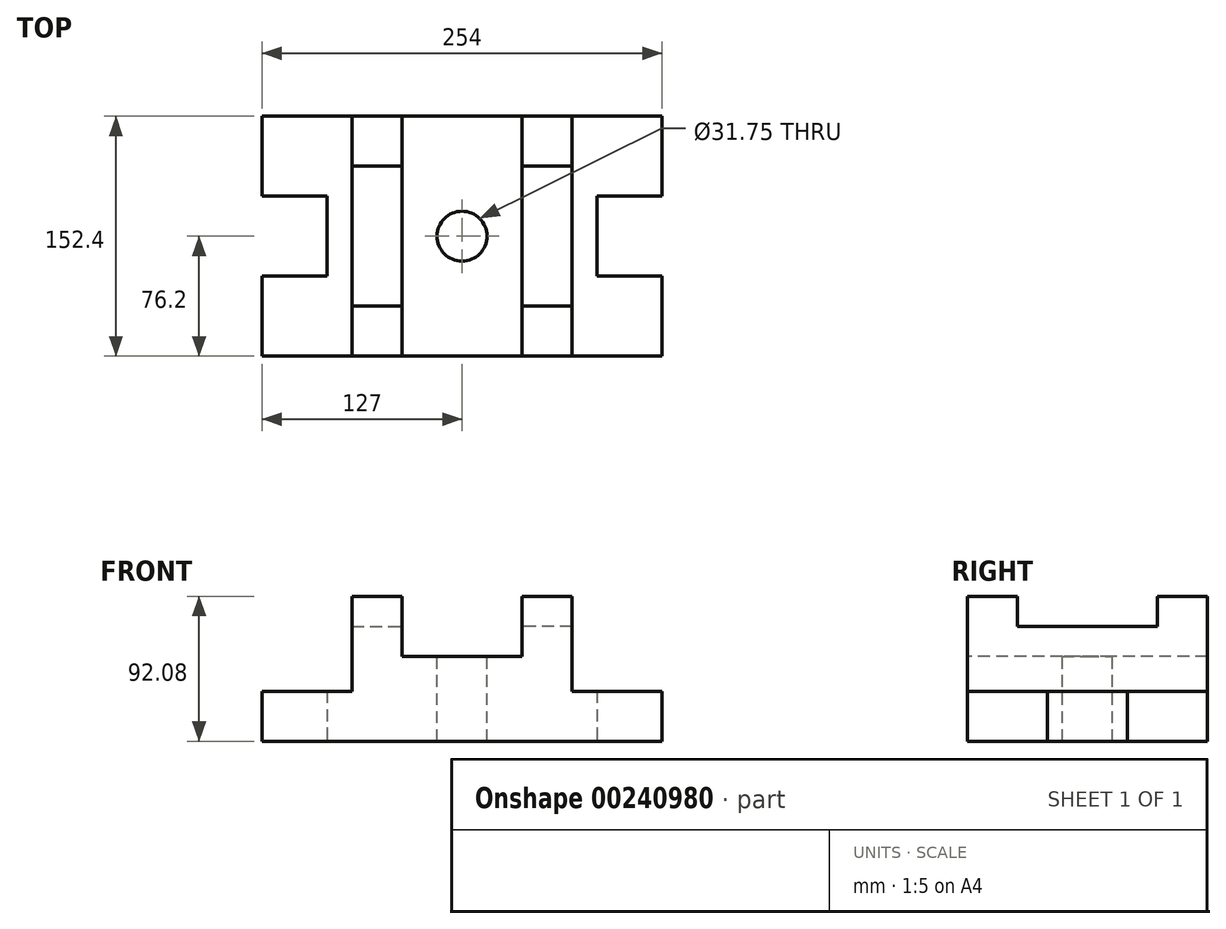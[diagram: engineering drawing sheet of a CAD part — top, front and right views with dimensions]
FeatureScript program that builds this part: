
annotation { "Feature Type Name" : "Feature", "Feature Type Description" : "" }
export const myFeature = defineFeature(function(context is Context, id is Id, definition is map)
    precondition{}
    {
        {
            var Q0;
            Q0=qCreatedBy(makeId("Top.planeOp"),FACE);
            var sketch = newSketch(context, id + "F0", { "sketchPlane" : qUnion([Q0])});
            skLineSegment(sketch, "E0.top", {"start": v(0, -76.2) * mm, "end": v(127, -76.2) * mm});
            skLineSegment(sketch, "E0.right", {"start": v(127, -25.4) * mm, "end": v(127, -76.2) * mm});
            skLineSegment(sketch, "E1.MirrorCS", {"start": v(0, 76.2) * mm, "end": v(127, 76.2) * mm});
            skLineSegment(sketch, "E2.MirrorCS", {"start": v(127, 25.4) * mm, "end": v(127, 76.2) * mm});
            skPoint(sketch, "E3", {"position": v(85.73, 0) * mm});
            skLineSegment(sketch, "E4.bottom", {"start": v(127, 25.4) * mm, "end": v(85.72, 25.4) * mm});
            skLineSegment(sketch, "E4.top", {"start": v(127, -25.4) * mm, "end": v(85.73, -25.4) * mm});
            skLineSegment(sketch, "E4.right", {"start": v(85.72, 25.4) * mm, "end": v(85.73, -25.4) * mm});
            skLineSegment(sketch, "E5.MirrorCS", {"start": v(0, 76.2) * mm, "end": v(-127, 76.2) * mm});
            skLineSegment(sketch, "E6.MirrorCS", {"start": v(0, -76.2) * mm, "end": v(-127, -76.2) * mm});
            skLineSegment(sketch, "E7.MirrorCS", {"start": v(-127, 25.4) * mm, "end": v(-127, 76.2) * mm});
            skLineSegment(sketch, "E8.MirrorCS", {"start": v(-85.72, 25.4) * mm, "end": v(-85.73, -25.4) * mm});
            skLineSegment(sketch, "E9.MirrorCS", {"start": v(-127, 25.4) * mm, "end": v(-85.72, 25.4) * mm});
            skLineSegment(sketch, "E10.MirrorCS", {"start": v(-127, -25.4) * mm, "end": v(-85.73, -25.4) * mm});
            skLineSegment(sketch, "E11.MirrorCS", {"start": v(-127, -25.4) * mm, "end": v(-127, -76.2) * mm});
            skLineSegment(sketch, "E12.bottom", {"start": v(69.85, -76.2) * mm, "end": v(-69.85, -76.2) * mm});
            skPoint(sketch, "E12.middle", {"position": v(0, 0) * mm});
            skSolve(sketch);
        }
        {
            var Q0;
            Q0 = qSketchRegion(id + "F0", true);
            extrude(context, id + "F1", {"entities" : qUnion([Q0]), "depth" : 31.75 * mm});
        }
        {
            var Q0;
            Q0=makeQuery(id+"F1.opExtrude","CAP_FACE",FACE,{"disambiguationData":[OSD([sQuery(id+"F0.wireOp",EDGE,"pTGMPnu9-1J7j-vLpY-UZ5C-XiEDzq8Ojeuh"),sQuery(id+"F0.wireOp",EDGE,"E0.top"),sQuery(id+"F0.wireOp",EDGE,"E0.right"),sQuery(id+"F0.wireOp",EDGE,"E1.MirrorCS"),sQuery(id+"F0.wireOp",EDGE,"E2.MirrorCS"),sQuery(id+"F0.wireOp",EDGE,"E4.bottom"),sQuery(id+"F0.wireOp",EDGE,"E4.top"),sQuery(id+"F0.wireOp",EDGE,"E4.right"),sQuery(id+"F0.wireOp",EDGE,"E5.MirrorCS"),sQuery(id+"F0.wireOp",EDGE,"E6.MirrorCS"),sQuery(id+"F0.wireOp",EDGE,"E7.MirrorCS"),sQuery(id+"F0.wireOp",EDGE,"E8.MirrorCS"),sQuery(id+"F0.wireOp",EDGE,"E9.MirrorCS"),sQuery(id+"F0.wireOp",EDGE,"E10.MirrorCS"),sQuery(id+"F0.wireOp",EDGE,"E11.MirrorCS"),sQuery(id+"F0.wireOp",EDGE,"E12.bottom")])],"isStart":false});
            var sketch = newSketch(context, id + "F2", { "sketchPlane" : qUnion([Q0])});
            skLineSegment(sketch, "E13.bottom", {"start": v(69.85, -76.2) * mm, "end": v(-69.85, -76.2) * mm});
            skLineSegment(sketch, "E13.top", {"start": v(69.85, 76.2) * mm, "end": v(-69.85, 76.2) * mm});
            skLineSegment(sketch, "E13.left", {"start": v(69.85, -76.2) * mm, "end": v(69.85, 76.2) * mm});
            skLineSegment(sketch, "E13.right", {"start": v(-69.85, -76.2) * mm, "end": v(-69.85, 76.2) * mm});
            skPoint(sketch, "E13.middle", {"position": v(0, 0) * mm});
            skSolve(sketch);
        }
        {
            var Q0;
            Q0 = qSketchRegion(id + "F2", true);
            var Q1;
            Q1=sQuery(id+"F2.wireOp",EDGE,"E13.right");
            var Q2;
            Q2=sQuery(id+"F2.wireOp",EDGE,"E13.top");
            var Q3;
            Q3=sQuery(id+"F2.wireOp",EDGE,"E13.left");
            var Q4;
            Q4=sQuery(id+"F2.wireOp",EDGE,"E13.bottom");
            extrude(context, id + "F3", {"entities" : qUnion([Q0]), "operationType" : NewBodyOperationType.ADD, "surfaceEntities" : qUnion([Q1, Q2, Q3, Q4]), "depth" : 22.22 * mm});
        }
        {
            var Q0;
            Q0=makeQuery(id+"F3.opExtrude","CAP_FACE",FACE,{"disambiguationData":[OSD([sQuery(id+"F2.wireOp",EDGE,"E13.bottom"),sQuery(id+"F2.wireOp",EDGE,"E13.top"),sQuery(id+"F2.wireOp",EDGE,"E13.left"),sQuery(id+"F2.wireOp",EDGE,"E13.right")])],"isStart":false});
            var sketch = newSketch(context, id + "F4", { "sketchPlane" : qUnion([Q0])});
            skLineSegment(sketch, "E14.bottom", {"start": v(69.85, 76.2) * mm, "end": v(38.1, 76.2) * mm});
            skLineSegment(sketch, "E14.top", {"start": v(69.85, -76.2) * mm, "end": v(38.1, -76.2) * mm});
            skLineSegment(sketch, "E14.left", {"start": v(69.85, 76.2) * mm, "end": v(69.85, -76.2) * mm});
            skLineSegment(sketch, "E14.right", {"start": v(38.1, 76.2) * mm, "end": v(38.1, -76.2) * mm});
            skLineSegment(sketch, "E15.MirrorCS", {"start": v(-38.1, 76.2) * mm, "end": v(-38.1, -76.2) * mm});
            skLineSegment(sketch, "E16.MirrorCS", {"start": v(-69.85, 76.2) * mm, "end": v(-38.1, 76.2) * mm});
            skLineSegment(sketch, "E17.MirrorCS", {"start": v(-69.85, 76.2) * mm, "end": v(-69.85, -76.2) * mm});
            skLineSegment(sketch, "E18.MirrorCS", {"start": v(-69.85, -76.2) * mm, "end": v(-38.1, -76.2) * mm});
            skSolve(sketch);
        }
        {
            var Q0;
            Q0 = qSketchRegion(id + "F4", true);
            extrude(context, id + "F5", {"entities" : qUnion([Q0]), "operationType" : NewBodyOperationType.ADD, "depth" : 19.05 * mm});
        }
        {
            var Q0;
            Q0=makeQuery(id+"F5.opExtrude","CAP_FACE",FACE,{"disambiguationData":[OSD([sQuery(id+"F4.wireOp",EDGE,"E14.bottom"),sQuery(id+"F4.wireOp",EDGE,"E14.top"),sQuery(id+"F4.wireOp",EDGE,"E14.left"),sQuery(id+"F4.wireOp",EDGE,"E14.right")])],"isStart":false});
            var sketch = newSketch(context, id + "F6", { "sketchPlane" : qUnion([Q0])});
            skLineSegment(sketch, "E19", {"start": v(38.1, -76.2) * mm, "end": v(69.85, -76.2) * mm});
            skLineSegment(sketch, "E20", {"start": v(69.85, -76.2) * mm, "end": v(69.85, -44.45) * mm});
            skLineSegment(sketch, "E21", {"start": v(69.85, -44.45) * mm, "end": v(38.1, -44.45) * mm});
            skLineSegment(sketch, "E22", {"start": v(38.1, -44.45) * mm, "end": v(38.1, -76.2) * mm});
            skLineSegment(sketch, "E23.MirrorCS", {"start": v(-69.85, -44.45) * mm, "end": v(-38.1, -44.45) * mm});
            skLineSegment(sketch, "E24.MirrorCS", {"start": v(-38.1, -44.45) * mm, "end": v(-38.1, -76.2) * mm});
            skLineSegment(sketch, "E25.MirrorCS", {"start": v(-69.85, -76.2) * mm, "end": v(-69.85, -44.45) * mm});
            skLineSegment(sketch, "E26.MirrorCS", {"start": v(-38.1, -76.2) * mm, "end": v(-69.85, -76.2) * mm});
            skLineSegment(sketch, "E27.MirrorCS", {"start": v(69.85, 44.45) * mm, "end": v(38.1, 44.45) * mm});
            skLineSegment(sketch, "E28.MirrorCS", {"start": v(69.85, 76.2) * mm, "end": v(69.85, 44.45) * mm});
            skLineSegment(sketch, "E29.MirrorCS", {"start": v(38.1, 76.2) * mm, "end": v(69.85, 76.2) * mm});
            skLineSegment(sketch, "E30.MirrorCS", {"start": v(38.1, 44.45) * mm, "end": v(38.1, 76.2) * mm});
            skLineSegment(sketch, "E31.MirrorCS", {"start": v(-69.85, 44.45) * mm, "end": v(-38.1, 44.45) * mm});
            skLineSegment(sketch, "E32.MirrorCS", {"start": v(-38.1, 44.45) * mm, "end": v(-38.1, 76.2) * mm});
            skLineSegment(sketch, "E33.MirrorCS", {"start": v(-69.85, 76.2) * mm, "end": v(-69.85, 44.45) * mm});
            skLineSegment(sketch, "E34", {"start": v(-69.85, 76.2) * mm, "end": v(-38.1, 76.2) * mm});
            skLineSegment(sketch, "E35", {"start": v(-69.85, -76.2) * mm, "end": v(-38.1, -76.2) * mm});
            skSolve(sketch);
        }
        {
            var Q0;
            Q0 = qSketchRegion(id + "F6", true);
            extrude(context, id + "F7", {"entities" : qUnion([Q0]), "operationType" : NewBodyOperationType.ADD, "depth" : 19.05 * mm});
        }
        {
            var Q0;
            Q0=makeQuery(id+"F3.opExtrude","CAP_FACE",FACE,{"disambiguationData":[OSD([sQuery(id+"F2.wireOp",EDGE,"E13.bottom"),sQuery(id+"F2.wireOp",EDGE,"E13.top"),sQuery(id+"F2.wireOp",EDGE,"E13.left"),sQuery(id+"F2.wireOp",EDGE,"E13.right")])],"isStart":false});
            var sketch = newSketch(context, id + "F8", { "sketchPlane" : qUnion([Q0])});
            skCircle(sketch, "E36", {"center": v(0, 0) * mm, "radius": 15.88 * mm});
            skSolve(sketch);
        }
        {
            var Q0;
            Q0 = qSketchRegion(id + "F8", true);
            extrude(context, id + "F9", {"entities" : qUnion([Q0]), "operationType" : NewBodyOperationType.REMOVE, "endBound" : BoundingType.THROUGH_ALL, "oppositeDirection" : true, "depth" : 50.8 * mm});
        }
    });
